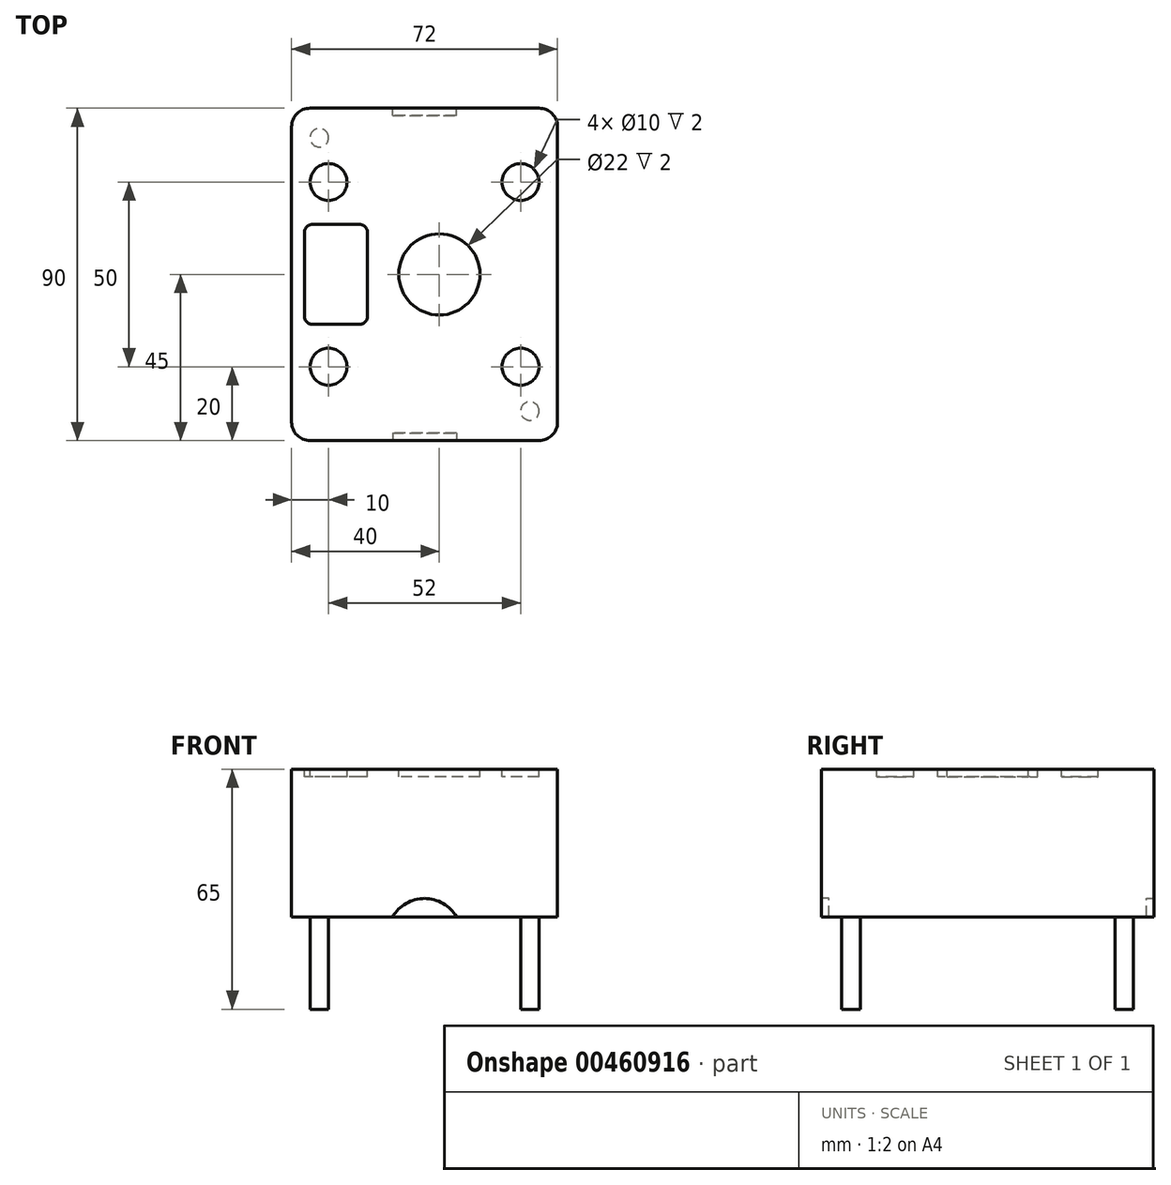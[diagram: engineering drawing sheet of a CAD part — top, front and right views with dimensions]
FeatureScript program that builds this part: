
annotation { "Feature Type Name" : "Feature", "Feature Type Description" : "" }
export const myFeature = defineFeature(function(context is Context, id is Id, definition is map)
    precondition{}
    {
        {
            var Q0;
            Q0=qCreatedBy(makeId("Top.planeOp"),FACE);
            var sketch = newSketch(context, id + "F0", { "sketchPlane" : qUnion([Q0])});
            skLineSegment(sketch, "E0.bottom", {"start": v(31, -45) * mm, "end": v(-31, -45) * mm});
            skLineSegment(sketch, "E0.top", {"start": v(31, 45) * mm, "end": v(-31, 45) * mm});
            skLineSegment(sketch, "E0.left", {"start": v(36, -40) * mm, "end": v(36, 40) * mm});
            skLineSegment(sketch, "E0.right", {"start": v(-36, -40) * mm, "end": v(-36, 40) * mm});
            skPoint(sketch, "E0.middle", {"position": v(0, 0) * mm});
            skPoint(sketch, "E1.visualSharp", {"position": v(-36, 45) * mm});
            skArc(sketch, "E1.filletArc", {"start": v(-31, 45) * mm, "mid": v(-34.54, 43.54) * mm, "end": v(-36, 40) * mm});
            skPoint(sketch, "E2.visualSharp", {"position": v(36, 45) * mm});
            skArc(sketch, "E2.filletArc", {"start": v(36, 40) * mm, "mid": v(34.54, 43.54) * mm, "end": v(31, 45) * mm});
            skPoint(sketch, "E3.visualSharp", {"position": v(36, -45) * mm});
            skArc(sketch, "E3.filletArc", {"start": v(31, -45) * mm, "mid": v(34.54, -43.54) * mm, "end": v(36, -40) * mm});
            skPoint(sketch, "E4.visualSharp", {"position": v(-36, -45) * mm});
            skArc(sketch, "E4.filletArc", {"start": v(-36, -40) * mm, "mid": v(-34.54, -43.54) * mm, "end": v(-31, -45) * mm});
            skSolve(sketch);
        }
        {
            var Q0;
            Q0=makeQuery(id+"F0.imprint","IMPRINT",FACE,{"disambiguationData":[TD([[makeQuery(id+"F0.imprint","IMPRINT",EDGE,{"derivedFrom":sQuery(id+"F0.wireOp",EDGE,"E0.bottom")}),-1.0]])]});
            extrude(context, id + "F1", {"entities" : qUnion([Q0]), "depth" : 65 * mm, "offsetDistance" : 25 * mm});
        }
        {
            var Q0;
            Q0=makeQuery(id+"F1.opExtrude","CAP_FACE",FACE,{"disambiguationData":[OSD([sQuery(id+"F0.wireOp",EDGE,"E0.bottom"),sQuery(id+"F0.wireOp",EDGE,"E0.top"),sQuery(id+"F0.wireOp",EDGE,"E0.left"),sQuery(id+"F0.wireOp",EDGE,"E0.right"),sQuery(id+"F0.wireOp",EDGE,"E1.filletArc"),sQuery(id+"F0.wireOp",EDGE,"E2.filletArc"),sQuery(id+"F0.wireOp",EDGE,"E3.filletArc"),sQuery(id+"F0.wireOp",EDGE,"E4.filletArc")])],"isStart":false});
            var sketch = newSketch(context, id + "F2", { "sketchPlane" : qUnion([Q0])});
            skCircle(sketch, "E5", {"center": v(4, 0) * mm, "radius": 11 * mm});
            skLineSegment(sketch, "E6", {"start": v(4, 0) * mm, "end": v(-24, 0) * mm, "construction": true});
            skLineSegment(sketch, "E7.bottom", {"start": v(-17.5, 13.5) * mm, "end": v(-30.5, 13.5) * mm});
            skLineSegment(sketch, "E7.top", {"start": v(-17.5, -13.5) * mm, "end": v(-30.5, -13.5) * mm});
            skLineSegment(sketch, "E7.left", {"start": v(-15.5, 11.5) * mm, "end": v(-15.5, -11.5) * mm});
            skLineSegment(sketch, "E7.right", {"start": v(-32.5, 11.5) * mm, "end": v(-32.5, -11.5) * mm});
            skPoint(sketch, "E7.middle", {"position": v(-24, 0) * mm});
            skPoint(sketch, "E8.visualSharp", {"position": v(-32.5, 13.5) * mm});
            skArc(sketch, "E8.filletArc", {"start": v(-30.5, 13.5) * mm, "mid": v(-31.91, 12.91) * mm, "end": v(-32.5, 11.5) * mm});
            skPoint(sketch, "E9.visualSharp", {"position": v(-15.5, 13.5) * mm});
            skArc(sketch, "E9.filletArc", {"start": v(-15.5, 11.5) * mm, "mid": v(-16.09, 12.91) * mm, "end": v(-17.5, 13.5) * mm});
            skPoint(sketch, "E10.visualSharp", {"position": v(-15.5, -13.5) * mm});
            skArc(sketch, "E10.filletArc", {"start": v(-17.5, -13.5) * mm, "mid": v(-16.09, -12.91) * mm, "end": v(-15.5, -11.5) * mm});
            skPoint(sketch, "E11.visualSharp", {"position": v(-32.5, -13.5) * mm});
            skArc(sketch, "E11.filletArc", {"start": v(-32.5, -11.5) * mm, "mid": v(-31.91, -12.91) * mm, "end": v(-30.5, -13.5) * mm});
            skLineSegment(sketch, "E12.direction1", {"start": v(-32.5, -13.5) * mm, "end": v(-4.3, -13.5) * mm, "construction": true});
            skLineSegment(sketch, "E12.direction2", {"start": v(-32.5, -13.5) * mm, "end": v(-32.5, -43.5) * mm, "construction": true});
            skCircle(sketch, "E13", {"center": v(-26, 25) * mm, "radius": 5 * mm});
            skCircle(sketch, "E14.MirrorC", {"center": v(26, 25) * mm, "radius": 5 * mm});
            skCircle(sketch, "E15.MirrorC", {"center": v(26, -25) * mm, "radius": 5 * mm});
            skCircle(sketch, "E16.MirrorC", {"center": v(-26, -25) * mm, "radius": 5 * mm});
            skSolve(sketch);
        }
        {
            var Q0;
            Q0 = qSketchRegion(id + "F2", true);
            extrude(context, id + "F3", {"entities" : qUnion([Q0]), "operationType" : NewBodyOperationType.REMOVE, "oppositeDirection" : true, "depth" : 2 * mm, "offsetDistance" : 25 * mm});
        }
        {
            var Q0;
            Q0=makeQuery(id+"F1.opExtrude","SWEPT_FACE",FACE,{"disambiguationData":[OSD([sQuery(id+"F0.wireOp",EDGE,"E0.bottom")])]});
            var sketch = newSketch(context, id + "F4", { "sketchPlane" : qUnion([Q0])});
            skCircle(sketch, "E17", {"center": v(0, 20) * mm, "radius": 10 * mm});
            skSolve(sketch);
        }
        {
            var Q0;
            Q0=makeQuery(id+"F4.imprint","IMPRINT",FACE,{"disambiguationData":[TD([[makeQuery(id+"F4.imprint","IMPRINT",EDGE,{"derivedFrom":sQuery(id+"F4.wireOp",EDGE,"E17")}),1.0]])]});
            extrude(context, id + "F5", {"entities" : qUnion([Q0]), "operationType" : NewBodyOperationType.REMOVE, "oppositeDirection" : true, "depth" : 2 * mm, "offsetDistance" : 25 * mm});
        }
        {
            var Q0;
            Q0=makeQuery(id+"F1.opExtrude","SWEPT_FACE",FACE,{"disambiguationData":[OSD([sQuery(id+"F0.wireOp",EDGE,"E0.top")])]});
            var sketch = newSketch(context, id + "F6", { "sketchPlane" : qUnion([Q0])});
            skCircle(sketch, "E18", {"center": v(0, 20) * mm, "radius": 10 * mm});
            skSolve(sketch);
        }
        {
            var Q0;
            Q0=makeQuery(id+"F6.imprint","IMPRINT",FACE,{"disambiguationData":[TD([[makeQuery(id+"F6.imprint","IMPRINT",EDGE,{"derivedFrom":sQuery(id+"F6.wireOp",EDGE,"E18")}),1.0]])]});
            extrude(context, id + "F7", {"entities" : qUnion([Q0]), "operationType" : NewBodyOperationType.REMOVE, "oppositeDirection" : true, "depth" : 2 * mm, "offsetDistance" : 25 * mm});
        }
        {
            var Q0;
            Q0=makeQuery(id+"F1.opExtrude","CAP_FACE",FACE,{"disambiguationData":[OSD([sQuery(id+"F0.wireOp",EDGE,"E0.bottom"),sQuery(id+"F0.wireOp",EDGE,"E0.top"),sQuery(id+"F0.wireOp",EDGE,"E0.left"),sQuery(id+"F0.wireOp",EDGE,"E0.right"),sQuery(id+"F0.wireOp",EDGE,"E1.filletArc"),sQuery(id+"F0.wireOp",EDGE,"E2.filletArc"),sQuery(id+"F0.wireOp",EDGE,"E3.filletArc"),sQuery(id+"F0.wireOp",EDGE,"E4.filletArc")])],"isStart":true});
            var sketch = newSketch(context, id + "F8", { "sketchPlane" : qUnion([Q0])});
            skCircle(sketch, "E19", {"center": v(28.5, -37) * mm, "radius": 2.5 * mm});
            skCircle(sketch, "E20.MirrorC", {"center": v(-28.5, -37) * mm, "radius": 2.5 * mm});
            skCircle(sketch, "E21.MirrorC", {"center": v(-28.5, 37) * mm, "radius": 2.5 * mm});
            skCircle(sketch, "E22.MirrorC", {"center": v(28.5, 37) * mm, "radius": 2.5 * mm});
            skSolve(sketch);
        }
        {
            var Q0;
            Q0=makeQuery(id+"F8.imprint","IMPRINT",FACE,{"disambiguationData":[TD([[makeQuery(id+"F8.imprint","IMPRINT",EDGE,{"derivedFrom":sQuery(id+"F8.wireOp",EDGE,"E19")}),1.0]])]});
            var Q1;
            Q1=makeQuery(id+"F8.imprint","IMPRINT",FACE,{"disambiguationData":[TD([[makeQuery(id+"F8.imprint","IMPRINT",EDGE,{"derivedFrom":sQuery(id+"F8.wireOp",EDGE,"E20.MirrorC")}),-1.0]])]});
            var Q2;
            Q2=makeQuery(id+"F8.imprint","IMPRINT",FACE,{"disambiguationData":[TD([[makeQuery(id+"F8.imprint","IMPRINT",EDGE,{"derivedFrom":sQuery(id+"F8.wireOp",EDGE,"E21.MirrorC")}),1.0]])]});
            var Q3;
            Q3=makeQuery(id+"F8.imprint","IMPRINT",FACE,{"disambiguationData":[TD([[makeQuery(id+"F8.imprint","IMPRINT",EDGE,{"derivedFrom":sQuery(id+"F8.wireOp",EDGE,"E22.MirrorC")}),-1.0]])]});
            extrude(context, id + "F9", {"entities" : qUnion([Q0, Q1, Q2, Q3]), "operationType" : NewBodyOperationType.REMOVE, "oppositeDirection" : true, "depth" : 25 * mm, "offsetDistance" : 25 * mm});
        }
    });
